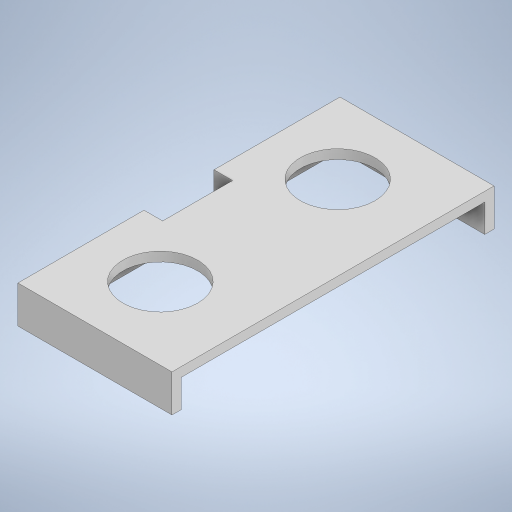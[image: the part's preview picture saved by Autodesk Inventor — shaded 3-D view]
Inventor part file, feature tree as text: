
AUTODESK INVENTOR PART (.ipt)
format: ipt  version: 2023 (Build 270158000, 158)  size: 280,064 bytes
history: native  units: mm
features: extrude x4, sketch x4
ambient origin geometry x8: Origin, YZ Plane, XZ Plane, XY Plane, X Axis, Y Axis, Z Axis, Center Point
bodies: Solid1 (feature_tree)
feature tree (8):
  extrude  "Extrusion1"  Depth=2.0mm
  extrude  "Extrusion2"  Depth=33.0mm
  extrude  "Extrusion3"  TaperAngle=0.0deg  [1 undecoded]
  extrude  "Extrusion4"  Depth=2.0mm TaperAngle=0.0deg
  sketch  "Sketch1"  dims[d0=2.0mm d1=2.0mm]
  sketch  "Sketch2"  dims[d3=2.0mm d4=33.0mm]
  sketch  "Sketch3"  dims[d5=69.0mm d7=0.0mm]
  sketch  "Sketch4"  dims[d8=6.0mm d9=0.0mm d10=2.0mm d11=0.0mm d12=16.0mm d13=16.0mm d14=34.5mm d15=19.0mm d16=19.0mm d17=15.0mm d18=15.0mm d19=2.0mm d20=0.0mm d21=15.0mm d22=27.0mm d23=8.0mm d24=4.0mm d25=0.0mm d26=0.5mm d27=0.872665mm d28=0.5mm d29=0.872665mm]
note: 1 required parameter value undecoded (feature->parameter linkage not recoverable at this tier; creation-order binding heuristic only, values carry confidence <= 0.55)
